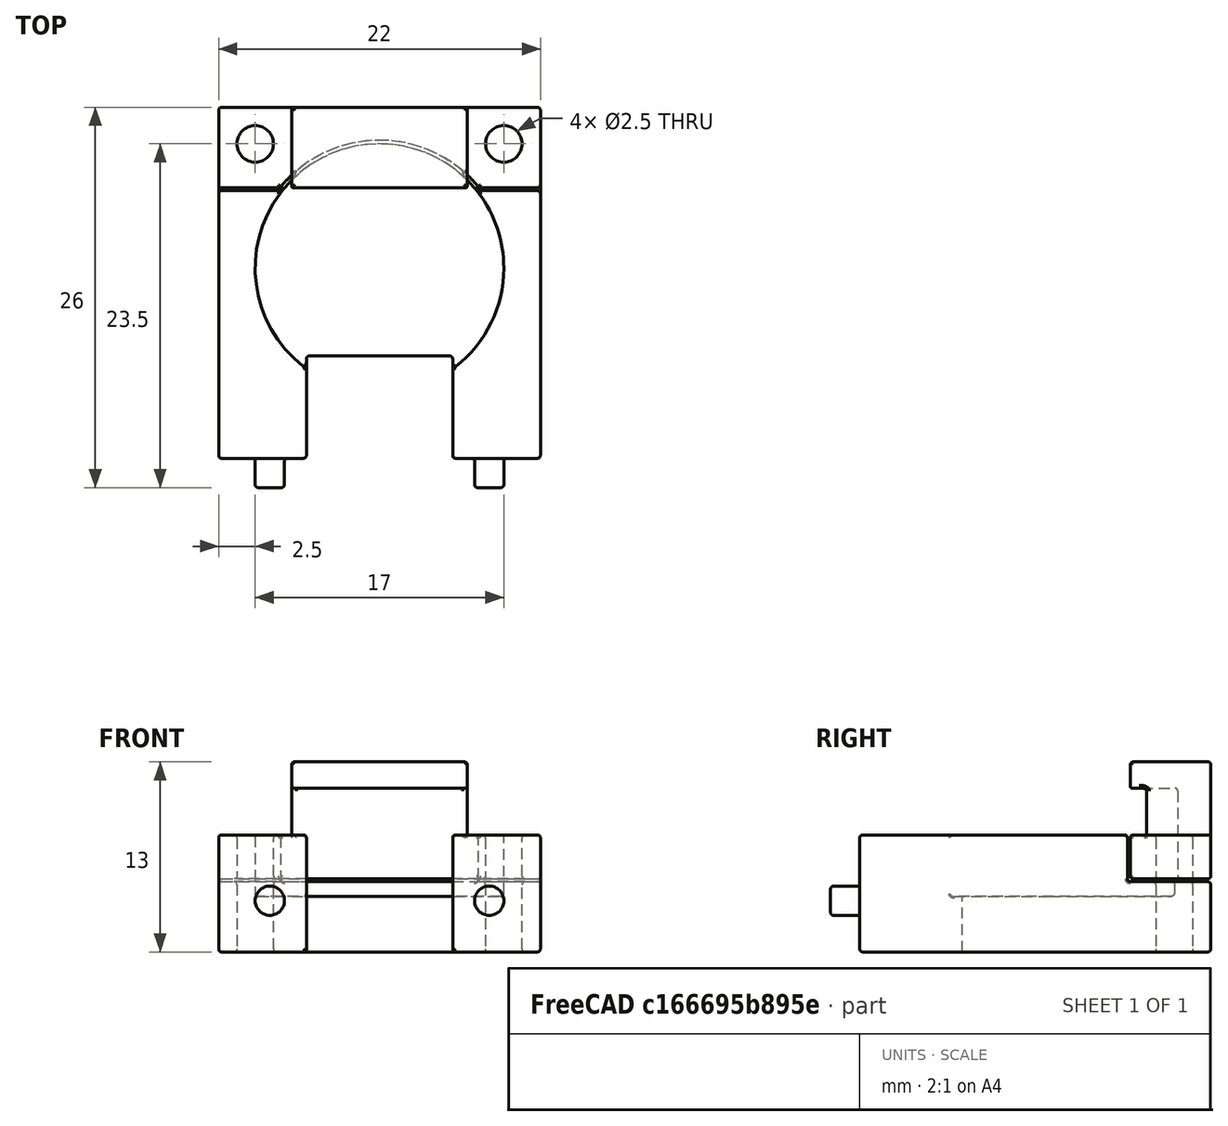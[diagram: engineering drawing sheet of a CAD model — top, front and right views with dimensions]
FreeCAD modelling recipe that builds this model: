
FCSTD DOCUMENT  (FreeCAD 1.0RUnknown)
Label: pot-socket
License: All rights reserved
LicenseURL: http://en.wikipedia.org/wiki/All_rights_reserved
objects: Part::Fillet×10, Part::Cylinder×8, Part::Cut×7, Part::Box×5, Part::Fuse×3, Part::MultiFuse×1, Mesh::Feature×1
note: 34 computed .brp shape members not serialized (recipe doc carries the construction recipe); baked Part::Feature solids carry a one-line shape summary decoded from their .brp

FEATURE [Part::Box] Box  label="Cube"
  AttacherType = Attacher::AttachEngine3D
  Height = 8
  Length = 22
  Placement = pos=(-11,-13,-1) rot=(0,0,1;0rad)
  Width = 24
FEATURE [Part::Box] Box001  label="Space between arms"
  AttacherType = Attacher::AttachEngine3D
  Height = 10
  Length = 10
  Placement = pos=(-5,-13,-2) rot=(0,0,1;0rad)
  Width = 7
FEATURE [Part::Cut] Cut
  Base = -> Box
  Tool = -> Box001
FEATURE [Part::Box] Box004  label="Rear Space with tolerance"
  AttacherType = Attacher::AttachEngine3D
  Height = 10
  Length = 24
  Placement = pos=(-12,5.3,3.8) rot=(0,0,1;0rad)
  Width = 5.7
FEATURE [Part::Cut] Cut001
  Base = -> Cut
  Tool = -> Box004
FEATURE [Part::Cylinder] Cylinder007
  Angle = 360
  AttacherType = Attacher::AttachEngine3D
  FirstAngle = 0
  Height = 2
  Placement = pos=(7.5,-10,2.5) rot=(1,0,0;1.5708rad)
  Radius = 1
  SecondAngle = 0
FEATURE [Part::Cylinder] Cylinder008  label="Pot Body with tolerance002"
  Angle = 360
  AttacherType = Attacher::AttachEngine3D
  FirstAngle = 0
  Height = 7.2
  Placement = pos=(0,0,2.8) rot=(0,0,1;0rad)
  Radius = 8.5
  SecondAngle = 0
FEATURE [Part::Cylinder] Cylinder009
  Angle = 360
  AttacherType = Attacher::AttachEngine3D
  FirstAngle = 0
  Height = 2
  Placement = pos=(-7.5,-10,2.5) rot=(1,0,0;1.5708rad)
  Radius = 1
  SecondAngle = 0
FEATURE [Part::Fuse] Fusion002
  Base = -> Cylinder007
  Placement = pos=(0,-3,0) rot=(0,0,1;0rad)
  Tool = -> Cylinder009
FEATURE [Part::MultiFuse] Fusion003
  Shapes = -> [Fusion002,Cut001]
FEATURE [Part::Fillet] Fillet011
  Base = -> Fusion003
  EdgeLinks = -> Fusion003 [Edge2,Edge3,Edge4,Edge5,Edge6,Edge7,Edge8,Edge9,?Edge26,?Edge31,?Edge30,Edge13,Edge14,Edge15,Edge16,Edge17,Edge18,Edge19,Edge20,Edge21,Edge22,Edge23,Edge24,Edge25,Edge26,Edge27,Edge28,Edge29,Edge30,Edge31,Edge32,Edge33,Edge34,Edge36]
  Edges = 34 edges r=0.2: [Edge2,Edge3,Edge4,Edge5,Edge6,Edge7,Edge8,Edge9,Edge26,Edge31,Edge30,Edge13,Edge14,Edge15,Edge16,Edge17,Edge18,Edge19,Edge20,Edge21,Edge22,Edge23,Edge24,Edge25,Edge26,Edge27,Edge28,Edge29,Edge30,Edge31,Edge32,Edge33,Edge34,Edge36]
FEATURE [Part::Fillet] Fillet012
  Base = -> Cylinder008
  EdgeLinks = -> Cylinder008 [Edge2]
  Edges = 1 edges r=0.2: [Edge2]
FEATURE [Part::Cut] Cut005
  Base = -> Fillet011
  Tool = -> Fillet012
FEATURE [Part::Cylinder] Cylinder010  label="M2 shaft 003"
  Angle = 360
  AttacherType = Attacher::AttachEngine3D
  FirstAngle = 0
  Height = 12
  Placement = pos=(8.5,8.5,-3) rot=(0,0,1;0rad)
  Radius = 1.25
  SecondAngle = 0
FEATURE [Part::Cylinder] Cylinder011  label="M2 shaft 004"
  Angle = 360
  AttacherType = Attacher::AttachEngine3D
  FirstAngle = 0
  Height = 12
  Placement = pos=(-8.5,8.5,-3) rot=(0,0,1;0rad)
  Radius = 1.25
  SecondAngle = 0
FEATURE [Part::Box] Box011  label="Rear Space002"
  AttacherType = Attacher::AttachEngine3D
  Height = 3
  Length = 22
  Placement = pos=(-11,5.5,4) rot=(0,0,1;0rad)
  Width = 5.5
FEATURE [Part::Box] Box012  label="Cube007"
  AttacherType = Attacher::AttachEngine3D
  Height = 6
  Length = 12
  Placement = pos=(-6,5.5,6) rot=(0,0,1;0rad)
  Width = 5.5
FEATURE [Part::Cylinder] Cylinder015  label="M2 shaft 007"
  Angle = 360
  AttacherType = Attacher::AttachEngine3D
  FirstAngle = 0
  Height = 12
  Placement = pos=(-8.5,8.5,-3) rot=(0,0,1;0rad)
  Radius = 1.25
  SecondAngle = 0
FEATURE [Part::Cylinder] Cylinder016  label="M2 shaft 008"
  Angle = 360
  AttacherType = Attacher::AttachEngine3D
  FirstAngle = 0
  Height = 12
  Placement = pos=(8.5,8.5,-3) rot=(0,0,1;0rad)
  Radius = 1.25
  SecondAngle = 0
FEATURE [Part::Cylinder] Cylinder017  label="Pot Body with tolerance004"
  Angle = 360
  AttacherType = Attacher::AttachEngine3D
  FirstAngle = 0
  Height = 9.2
  Placement = pos=(0,0,3) rot=(0,0,1;0rad)
  Radius = 8.75
  SecondAngle = 0
FEATURE [Part::Fillet] Fillet024  label="Pot Body with tolerance fillited002"
  Base = -> Cylinder017
  EdgeLinks = -> Cylinder017 [Edge2,Edge3]
  Edges = 2 edges: [Edge2 r=0.5,Edge3 r=0.2]
  Placement = pos=(0,0,-3) rot=(0,0,1;0rad)
FEATURE [Part::Fuse] Fusion005
  Base = -> Box011
  Tool = -> Box012
FEATURE [Part::Cut] Cut011
  Base = -> Fusion005
  Tool = -> Cylinder015
FEATURE [Part::Cut] Cut012
  Base = -> Cut011
  Placement = pos=(0,0,-1) rot=(0,0,1;0rad)
  Tool = -> Cylinder016
FEATURE [Part::Cut] Cut013  label="Shell Cut"
  Base = -> Cut012
  Placement = pos=(0,0,1) rot=(0,0,1;0rad)
  Tool = -> Fillet024
FEATURE [Part::Fillet] Fillet026
  Base = -> Cut013
  EdgeLinks = -> Cut013 [Edge1,Edge2,Edge3,Edge4,Edge6,Edge7,Edge8,Edge12,Edge13,Edge17,Edge18,Edge19,Edge34,Edge35,Edge36]
  Edges = 15 edges r=0.2: [Edge1,Edge2,Edge3,Edge4,Edge6,Edge7,Edge8,Edge12,Edge13,Edge17,Edge18,Edge19,Edge34,Edge35,Edge36]
FEATURE [Part::Fillet] Fillet027
  Base = -> Fillet026
  EdgeLinks = -> Fillet026 [Edge35,Edge49,Edge51,Edge55]
  Edges = 4 edges r=0.2: [Edge35,Edge49,Edge51,Edge55]
FEATURE [Part::Fillet] Fillet028
  Base = -> Fillet027
  EdgeLinks = -> Fillet027 [Edge23,Edge56,Edge57,Edge107]
  Edges = 4 edges r=0.2: [Edge23,Edge56,Edge57,Edge107]
FEATURE [Part::Fillet] Fillet029
  Base = -> Fillet028
  EdgeLinks = -> Fillet028 [Edge16,Edge43,Edge46,Edge47]
  Edges = 4 edges r=0.2: [Edge16,Edge43,Edge46,Edge47]
FEATURE [Part::Fillet] Fillet030  label="Shell"
  Base = -> Fillet029
  EdgeLinks = -> Fillet029 [Edge22]
  Edges = 1 edges r=0.1: [Edge22]
FEATURE [Part::Fuse] Fusion
  Base = -> Cylinder010
  Tool = -> Cylinder011
FEATURE [Part::Cut] Cut014
  Base = -> Cut005
  Tool = -> Fusion
FEATURE [Part::Fillet] Fillet
  Base = -> Cut014
  EdgeLinks = -> Cut014 [Edge32,Edge33,Edge78,Edge80]
  Edges = 4 edges r=0.2: [Edge32,Edge33,Edge78,Edge80]
FEATURE [Part::Fillet] Fillet031  label="Base"
  Base = -> Fillet
  EdgeLinks = -> Fillet [Edge17,Edge18,Edge19,Edge24,Edge29,Edge34,Edge41,Edge42,Edge43,Edge54,Edge57,Edge91,Edge94,Edge95,Edge96,Edge97,Edge98,Edge99,Edge100,Edge101,Edge102]
  Edges = 21 edges r=0.1: [Edge17,Edge18,Edge19,Edge24,Edge29,Edge34,Edge41,Edge42,Edge43,Edge54,Edge57,Edge91,Edge94,Edge95,Edge96,Edge97,Edge98,Edge99,Edge100,Edge101,Edge102]
FEATURE [Mesh::Feature] pcb
  Placement = pos=(100,-13,155.5) rot=(1,1,-1;2.0944rad)
